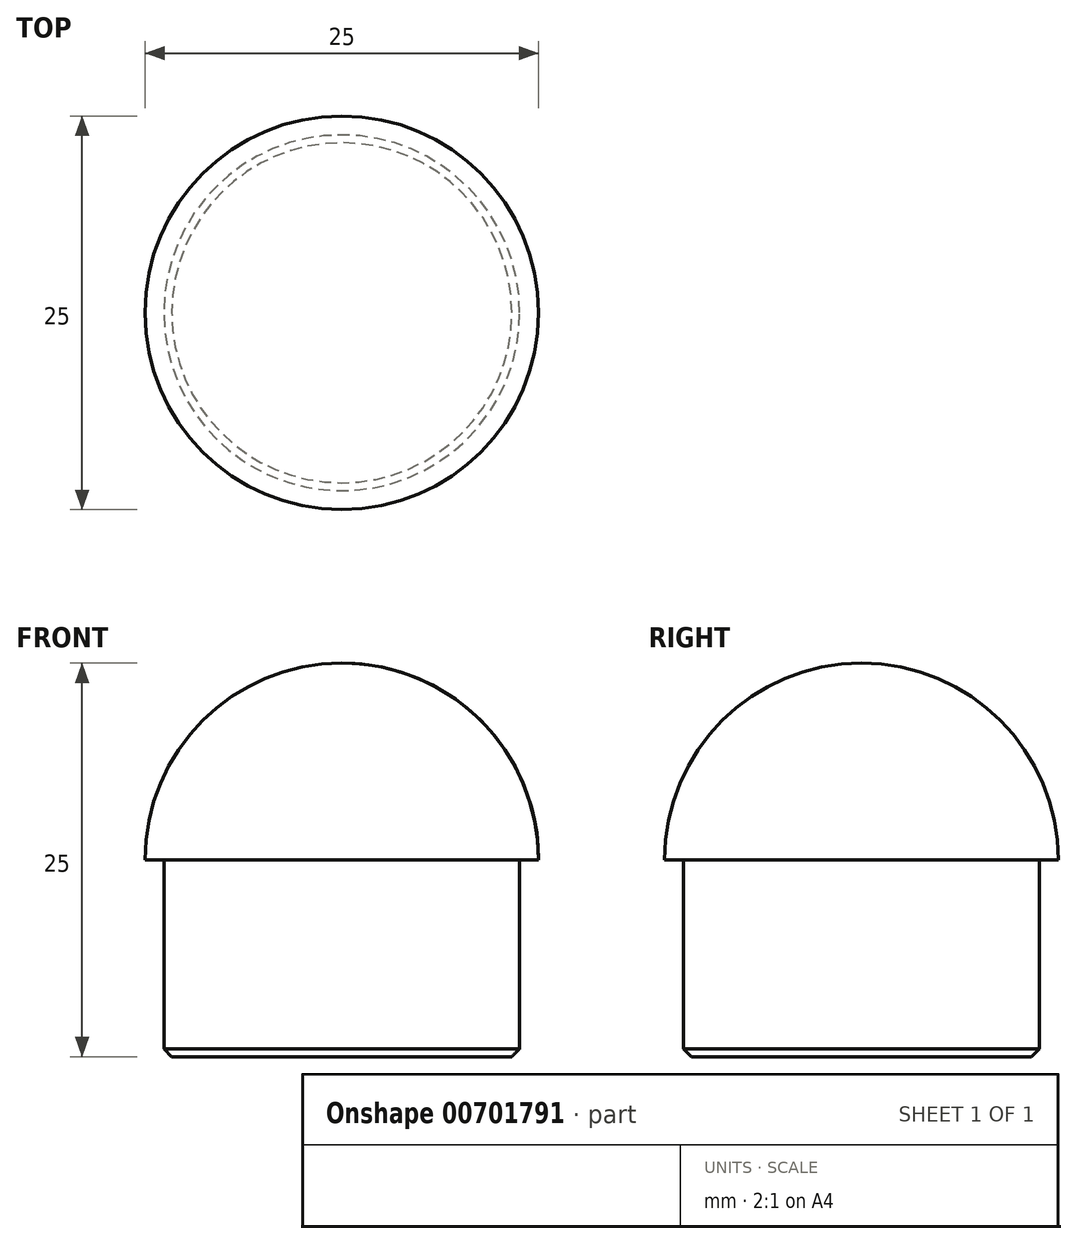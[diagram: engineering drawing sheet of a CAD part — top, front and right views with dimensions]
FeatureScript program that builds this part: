
annotation { "Feature Type Name" : "Feature", "Feature Type Description" : "" }
export const myFeature = defineFeature(function(context is Context, id is Id, definition is map)
    precondition{}
    {
        {
            var Q0;
            Q0=qCreatedBy(makeId("Top.planeOp"),FACE);
            var sketch = newSketch(context, id + "F0", { "sketchPlane" : qUnion([Q0])});
            skCircle(sketch, "E0", {"center": v(0, 0) * mm, "radius": 12.5 * mm});
            skSolve(sketch);
        }
        {
            var Q0;
            Q0=makeQuery(id+"F0.imprint","IMPRINT",FACE,{"disambiguationData":[TD([[makeQuery(id+"F0.imprint","IMPRINT",EDGE,{"derivedFrom":sQuery(id+"F0.wireOp",EDGE,"E0")}),1.0]])]});
            extrude(context, id + "F1", {"entities" : qUnion([Q0]), "depth" : 12.5 * mm, "offsetDistance" : 25 * mm});
        }
        {
            var Q0;
            Q0=makeQuery(id+"F1.opExtrude","CAP_EDGE",EDGE,{"disambiguationData":[OSD([sQuery(id+"F0.wireOp",EDGE,"E0")])],"isStart":false});
            fillet(context, id + "F2", {"entities" : qUnion([Q0]), "radius" : 12.5 * mm, "tangentPropagation" : true, "allowEdgeOverflow" : false});
        }
        {
            var Q0;
            Q0=qCreatedBy(makeId("Top.planeOp"),FACE);
            var sketch = newSketch(context, id + "F3", { "sketchPlane" : qUnion([Q0])});
            skCircle(sketch, "E1", {"center": v(0, 0) * mm, "radius": 11.3 * mm});
            skSolve(sketch);
        }
        {
            var Q0;
            Q0=makeQuery(id+"F3.imprint","IMPRINT",FACE,{"disambiguationData":[TD([[makeQuery(id+"F3.imprint","IMPRINT",EDGE,{"derivedFrom":sQuery(id+"F3.wireOp",EDGE,"E1")}),1.0]])]});
            extrude(context, id + "F4", {"entities" : qUnion([Q0]), "operationType" : NewBodyOperationType.ADD, "oppositeDirection" : true, "depth" : 12.5 * mm, "offsetDistance" : 25 * mm});
        }
        {
            var Q0;
            Q0=makeQuery(id+"F4.opExtrude","CAP_EDGE",EDGE,{"disambiguationData":[OSD([sQuery(id+"F3.wireOp",EDGE,"E1")])],"isStart":false});
            chamfer(context, id + "F5", {"entities" : qUnion([Q0]), "width" : 0.5 * mm, "tangentPropagation" : true});
        }
    });
